# Revit family: Furniture-Wall_Mount-Vanity-KOHLER-Maxstow-K-34654
name_source: partatom
category: Plumbing Fixtures
units: mm (PartAtom-declared; Revit-internal decimal feet)

## family parameters
Cut with Voids When Loaded = No
Host = Face
OmniClass Number = 23.21.19.15.33
OmniClass Title = Residential Specialty Casework
Part Type = Normal
Room Calculation Point = No
Round Connector Dimension = Use Diameter
Shared = No

## types (4) — shared parameters
ADA Compliant = No
Assembly Code = D2010400
CW Connection = No
Cold Water Inlet = Cold Water Inlet
Date Modified = 04/21/2023
Default Elevation = 35"
Description = 30 Inch Bathroom Vanity Set
Drain Included = No
HW Connection = No
Height = 23 3/8"
Hot Water Inlet = Hot Water Inlet
Length = 22 11/16"
Manufacturer = Kohler Co.
Master Format 2014 = 12 35 30.23
Master Format 2014 Name = Bathroom Casework
Material = Solid Wood Construction
Product Documentation Link = https://www.us.kohler.com
Product Name = Maxstow
Product Page URL = http://www.us.kohler.com
URL = https://www.us.kohler.com
Vent Connection = No
Waste Connection = Yes
Waste Water Outlet = Waste Water Outlet
WaterSense Certified = No
Width = 31"

## per-type parameters (varying)
| type | Finish | Model | Secondary Finish | Type |
| DWG-Warm Dark Grey | KOHLER-Wood-DWG-Warm_Dark_Grey | K-34654-DWG | Kohler-Metal-BN-Vibrant_Brushed_Nickel | 1 |
| 0-White | Kohler-Wood-Molded-0-White | K-34654-0 | Kohler-Metal-CP-Polished_Chrome | 2 |
| AGA-Ash Grey | KOHLER-Wood-AGA-Ash_Grey | K-34654-AGA | Kohler-Metal-BN-Vibrant_Brushed_Nickel | 3 |
| WEK-Weathered Oak | KOHLER-Wood-WEK-Weathered_Oak | K-34654-WEK | Kohler-Metal-BN-Vibrant_Brushed_Nickel | 4 |

## geometry (parser evidence)
native form markers: Sweep x7
no freeform markers — native parametric forms only
